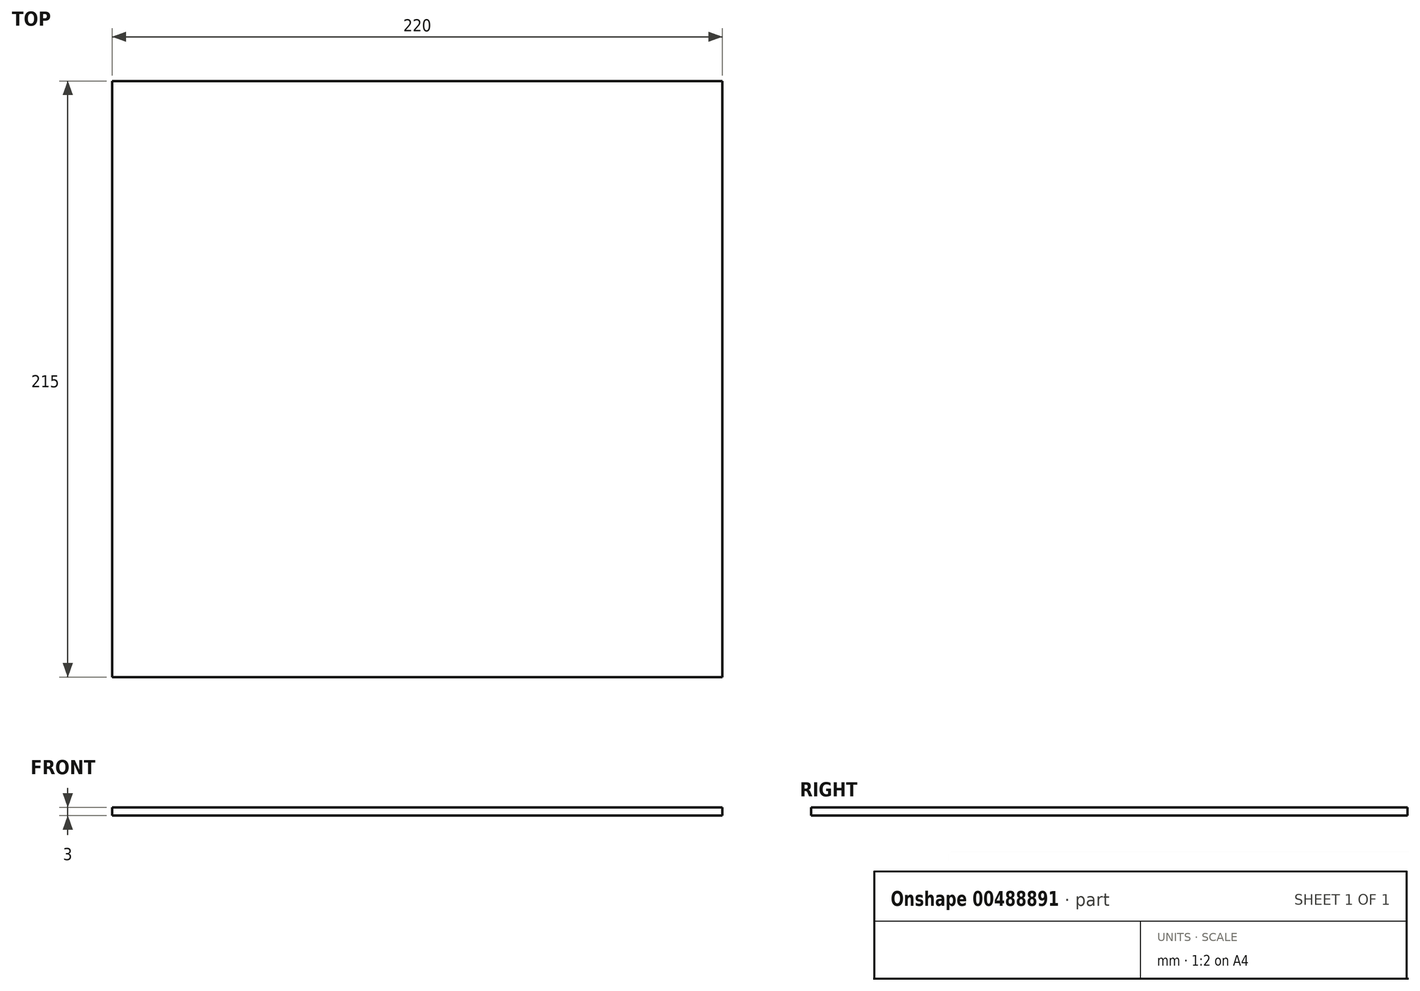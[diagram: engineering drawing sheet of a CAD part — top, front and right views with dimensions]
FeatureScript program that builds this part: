
annotation { "Feature Type Name" : "Feature", "Feature Type Description" : "" }
export const myFeature = defineFeature(function(context is Context, id is Id, definition is map)
    precondition{}
    {
        {
            var Q0;
            Q0=qCreatedBy(makeId("Top.planeOp"),FACE);
            var sketch = newSketch(context, id + "F0", { "sketchPlane" : qUnion([Q0])});
            skLineSegment(sketch, "E0.bottom", {"start": v(-112.94, 182.03) * mm, "end": v(107.06, 182.03) * mm});
            skLineSegment(sketch, "E0.top", {"start": v(-112.94, -32.97) * mm, "end": v(107.06, -32.97) * mm});
            skLineSegment(sketch, "E0.left", {"start": v(-112.94, 182.03) * mm, "end": v(-112.94, -32.97) * mm});
            skLineSegment(sketch, "E0.right", {"start": v(107.06, 182.03) * mm, "end": v(107.06, -32.97) * mm});
            skSolve(sketch);
        }
        {
            var Q0;
            Q0=makeQuery(id+"F0.imprint","IMPRINT",FACE,{"disambiguationData":[TD([[makeQuery(id+"F0.imprint","IMPRINT",EDGE,{"derivedFrom":sQuery(id+"F0.wireOp",EDGE,"E0.bottom")}),-1.0]])]});
            extrude(context, id + "F1", {"entities" : qUnion([Q0]), "depth" : 3 * mm});
        }
    });
